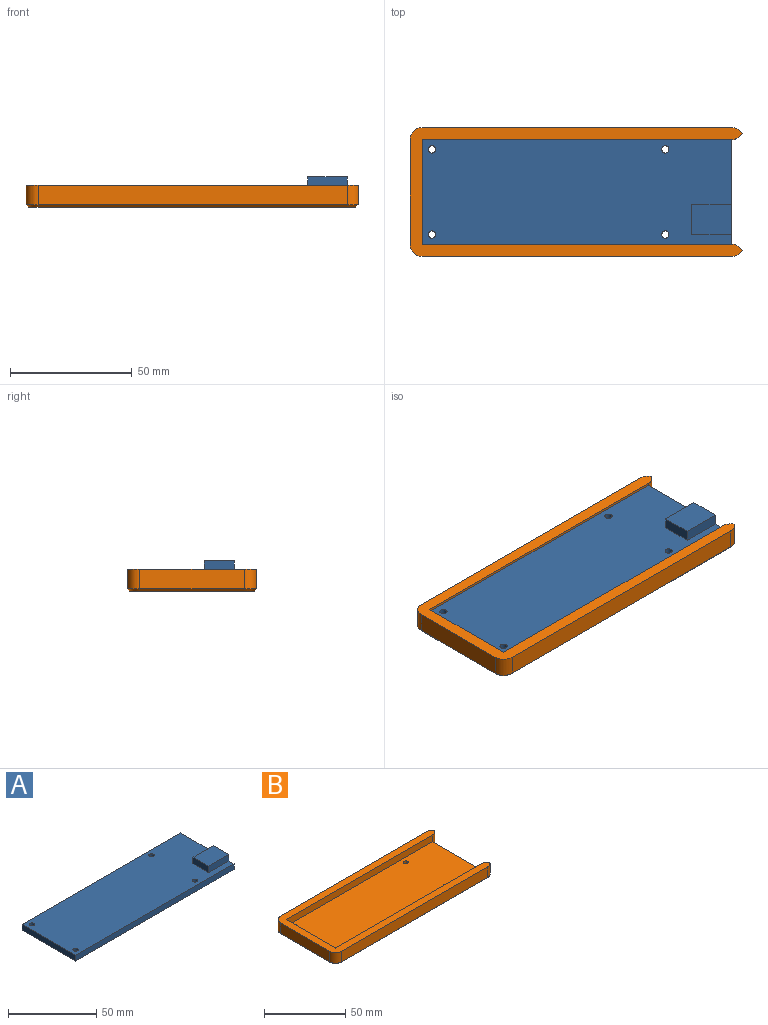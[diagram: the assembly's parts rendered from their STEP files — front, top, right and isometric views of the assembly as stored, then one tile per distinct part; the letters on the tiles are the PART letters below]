
ASSEMBLY  parts=2 mates=1
PART A: 14 faces, bbox 127.2x43x8.5 mm
  f0: plane 127.2x43mm, normal (0,0,1), area 5236.4mm2, adj f1,f2,f3,f4,f5,f6,f7,f8
  f1: plane 127.2x4mm, normal (0,-1,0), area 508.8mm2, adj f0,f2,f8,f9
  f2: plane 43x8.5mm, normal (1,0,0), area 228.2mm2, adj f0,f1,f3,f9,f10,f11,f13
  f3: plane 127.2x4mm, normal (0,1,0), area 508.8mm2, adj f0,f2,f8,f9
  f4: cylinder r=1.5mm len=4mm, axis (0,0,-1), area 37.7mm2, adj f0,f9
  f5: cylinder r=1.5mm len=4mm, axis (0,0,-1), area 37.7mm2, adj f0,f9
  f6: cylinder r=1.5mm len=4mm, axis (0,0,-1), area 37.7mm2, adj f0,f9
  f7: cylinder r=1.5mm len=4mm, axis (0,0,-1), area 37.7mm2, adj f0,f9
  f8: plane 43x4mm, normal (-1,0,0), area 172mm2, adj f0,f1,f3,f9
  f9: plane 127.2x43mm, normal (0,0,-1), area 5441.3mm2, adj f1,f2,f3,f4,f5,f6,f7,f8
  f10: plane 16.4x4.5mm, normal (0,-1,0), area 73.8mm2, adj f0,f2,f12,f13
  f11: plane 16.4x4.5mm, normal (0,1,0), area 73.8mm2, adj f0,f2,f12,f13
  f12: plane 12.5x4.5mm, normal (-1,0,0), area 56.2mm2, adj f0,f10,f11,f13
  f13: plane 16.4x12.5mm, normal (0,0,1), area 204.9mm2, adj f2,f10,f11,f12
PART B: 34 faces, bbox 136.5x53x9 mm
  f0: plane 43x3mm, normal (1,0,0), area 129mm2, adj f5,f15,f18,f20
  f1: cylinder r=1.5mm len=3mm, axis (0,0,-1), area 28.3mm2, adj f5,f33
  f2: cylinder r=1.5mm len=3mm, axis (0,0,-1), area 28.3mm2, adj f5,f32
  f3: cylinder r=1.5mm len=3mm, axis (0,0,-1), area 28.3mm2, adj f5,f31
  f4: cylinder r=1.5mm len=3mm, axis (0,0,-1), area 28.3mm2, adj f5,f30
  f5: plane 127.2x43mm, normal (0,0,1), area 5441.3mm2, adj f0,f1,f2,f3,f4,f7,f8,f12
  f6: plane 134.32x51mm, normal (0,0,-1), area 6573.8mm2, adj f20,f21,f22,f23,f24,f25,f26,f27
  f7: plane 43x5mm, normal (1,0,0), area 215mm2, adj f5,f8,f12,f13
  f8: plane 127.2x5mm, normal (0,1,0), area 636mm2, adj f5,f7,f13,f15
  f9: plane 127.2x8mm, normal (0,-1,0), area 1017.6mm2, adj f13,f14,f16,f25
  f10: plane 43x8mm, normal (-1,0,0), area 344mm2, adj f13,f16,f17,f29
  f11: plane 127.2x8mm, normal (0,1,0), area 1017.6mm2, adj f13,f17,f19,f26
  f12: plane 127.2x5mm, normal (0,-1,0), area 636mm2, adj f5,f7,f13,f18
  f13: plane 136.53x53mm, normal (0,0,1), area 1557mm2, adj f7,f8,f9,f10,f11,f12,f14,f15
  f14: cylinder r=5mm len=8mm, axis (0,0,1), area 41.9mm2, adj f9,f13,f15,f23
  f15: cylinder r=5mm len=8mm, axis (0,0,-1), area 41.9mm2, adj f0,f8,f13,f14,f21
  f16: cylinder r=5mm len=8mm, axis (0,0,-1), area 62.8mm2, adj f9,f10,f13,f27
  f17: cylinder r=5mm len=8mm, axis (0,0,1), area 62.8mm2, adj f10,f11,f13,f28
  f18: cylinder r=5mm len=8mm, axis (0,0,-1), area 41.9mm2, adj f0,f12,f13,f19,f22
  f19: cylinder r=5mm len=8mm, axis (0,0,-1), area 41.9mm2, adj f11,f13,f18,f24
  f20: plane 45.25x1mm, normal (0.71,0,-0.71), area 62.3mm2, adj f0,f6,f21,f22
  f21: cone r=4mm half-angle=45deg, axis (0,0,1), area 6.9mm2, adj f6,f15,f20,f23
  f22: cone r=4mm half-angle=45deg, axis (0,0,1), area 6.9mm2, adj f6,f18,f20,f24
  f23: cone r=4mm half-angle=45deg, axis (0,0,1), area 6.2mm2, adj f6,f14,f21,f25
  f24: cone r=4mm half-angle=45deg, axis (0,0,1), area 6.2mm2, adj f6,f19,f22,f26
  f25: plane 127.2x1mm, normal (0,-0.71,-0.71), area 179.9mm2, adj f6,f9,f23,f27
  f26: plane 127.2x1mm, normal (0,0.71,-0.71), area 179.9mm2, adj f6,f11,f24,f28
  f27: cone r=4mm half-angle=45deg, axis (0,0,1), area 10mm2, adj f6,f16,f25,f29
  f28: cone r=4mm half-angle=45deg, axis (0,0,1), area 10mm2, adj f6,f17,f26,f29
  f29: plane 43x1mm, normal (-0.71,0,-0.71), area 60.8mm2, adj f6,f10,f27,f28
  f30: cone r=2.5mm half-angle=45deg, axis (0,0,-1), area 17.8mm2, adj f4,f6
  f31: cone r=2.5mm half-angle=45deg, axis (0,0,-1), area 17.8mm2, adj f3,f6
  f32: cone r=2.5mm half-angle=45deg, axis (0,0,-1), area 17.8mm2, adj f2,f6
  f33: cone r=2.5mm half-angle=45deg, axis (0,0,-1), area 17.8mm2, adj f1,f6
PLACE A t=(0,63.37,4)mm
PLACE B at identity
MATE fastened A.f4 <-> B.f1  axis (0,0,-1) through (-59.6,45.87,4)mm
